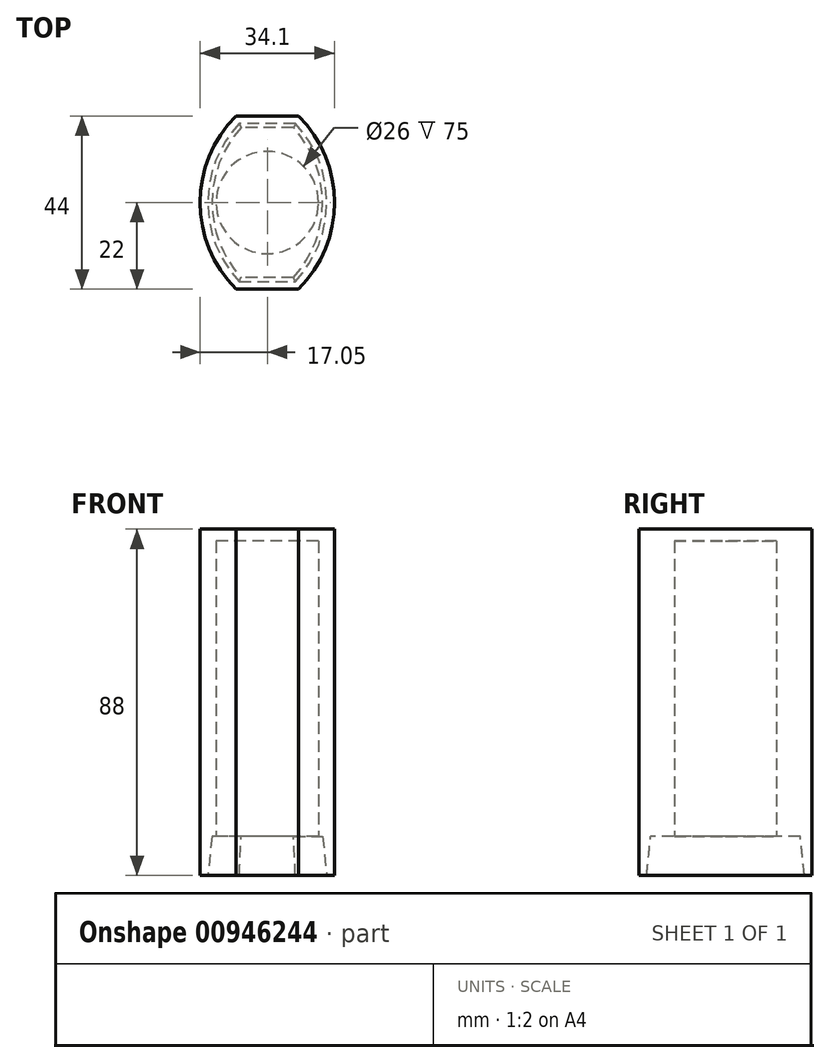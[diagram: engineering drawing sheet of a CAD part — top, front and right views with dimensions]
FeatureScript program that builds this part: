
annotation { "Feature Type Name" : "Feature", "Feature Type Description" : "" }
export const myFeature = defineFeature(function(context is Context, id is Id, definition is map)
    precondition{}
    {
        {
            var Q0;
            Q0=qCreatedBy(makeId("Top.planeOp"),FACE);
            var sketch = newSketch(context, id + "F0", { "sketchPlane" : qUnion([Q0])});
            skLineSegment(sketch, "E0.bottom", {"start": v(6.66, -19) * mm, "end": v(-6.66, -19) * mm});
            skLineSegment(sketch, "E0.top", {"start": v(6.66, 19) * mm, "end": v(-6.66, 19) * mm});
            skLineSegment(sketch, "E0.left", {"start": v(14.1, -19) * mm, "end": v(14.1, 19) * mm, "construction": true});
            skLineSegment(sketch, "E0.right", {"start": v(-14.1, -19) * mm, "end": v(-14.1, 19) * mm, "construction": true});
            skPoint(sketch, "E0.middle", {"position": v(0, 0) * mm});
            skArc(sketch, "E1", {"start": v(-6.66, 19) * mm, "mid": v(-14.05, 0) * mm, "end": v(-6.66, -19) * mm});
            skArc(sketch, "E2.MirrorCS", {"start": v(6.66, 19) * mm, "mid": v(14.05, 0) * mm, "end": v(6.66, -19) * mm});
            skArc(sketch, "E3.0", {"start": v(7.95, 22) * mm, "mid": v(17.05, 0) * mm, "end": v(7.95, -22) * mm});
            skLineSegment(sketch, "E3.1", {"start": v(7.95, 22) * mm, "end": v(-7.95, 22) * mm});
            skArc(sketch, "E3.2", {"start": v(-7.95, 22) * mm, "mid": v(-17.05, 0) * mm, "end": v(-7.95, -22) * mm});
            skLineSegment(sketch, "E3.3", {"start": v(7.95, -22) * mm, "end": v(-7.95, -22) * mm});
            skSolve(sketch);
        }
        {
            var Q0;
            Q0=makeQuery(id+"F0.imprint","IMPRINT",FACE,{"disambiguationData":[TD([[makeQuery(id+"F0.imprint","IMPRINT",EDGE,{"derivedFrom":sQuery(id+"F0.wireOp",EDGE,"E0.bottom")}),1.0]])]});
            extrude(context, id + "F1", {"entities" : qUnion([Q0]), "oppositeDirection" : true, "depth" : 10 * mm, "offsetDistance" : 25 * mm});
        }
        {
            var Q0;
            Q0=makeQuery(id+"F0.imprint","IMPRINT",FACE,{"disambiguationData":[TD([[makeQuery(id+"F0.imprint","IMPRINT",EDGE,{"derivedFrom":sQuery(id+"F0.wireOp",EDGE,"E0.bottom")}),-1.0]])]});
            extrude(context, id + "F2", {"entities" : qUnion([Q0]), "operationType" : NewBodyOperationType.REMOVE, "oppositeDirection" : true, "depth" : 15.1 * mm, "offsetDistance" : 25 * mm, "hasDraft" : true, "draftAngle" : 6 * degree});
        }
        {
            var Q0;
            Q0=makeQuery(id+"F1.opExtrude","CAP_FACE",FACE,{"disambiguationData":[OSD([sQuery(id+"F0.wireOp",EDGE,"E0.bottom"),sQuery(id+"F0.wireOp",EDGE,"E0.top"),sQuery(id+"F0.wireOp",EDGE,"E1"),sQuery(id+"F0.wireOp",EDGE,"E2.MirrorCS"),sQuery(id+"F0.wireOp",EDGE,"E3.0"),sQuery(id+"F0.wireOp",EDGE,"E3.1"),sQuery(id+"F0.wireOp",EDGE,"E3.2"),sQuery(id+"F0.wireOp",EDGE,"E3.3")])],"isStart":true});
            var sketch = newSketch(context, id + "F3", { "sketchPlane" : qUnion([Q0])});
            skCircle(sketch, "E4", {"center": v(0, 0) * mm, "radius": 13 * mm});
            skCircle(sketch, "E5.0", {"center": v(0, 0) * mm, "radius": 16 * mm});
            skLineSegment(sketch, "E6.0.0", {"start": v(-7.95, -22) * mm, "end": v(7.95, -22) * mm});
            skArc(sketch, "E6.0.1", {"start": v(7.95, -22) * mm, "mid": v(17.05, 0) * mm, "end": v(7.95, 22) * mm});
            skLineSegment(sketch, "E6.0.2", {"start": v(7.95, 22) * mm, "end": v(-7.95, 22) * mm});
            skArc(sketch, "E6.0.3", {"start": v(-7.95, 22) * mm, "mid": v(-17.05, 0) * mm, "end": v(-7.95, -22) * mm});
            skArc(sketch, "E7.0.0", {"start": v(6.66, -19) * mm, "mid": v(14.05, 0) * mm, "end": v(6.66, 19) * mm});
            skLineSegment(sketch, "E7.0.1", {"start": v(6.66, 19) * mm, "end": v(-6.66, 19) * mm});
            skArc(sketch, "E7.0.2", {"start": v(-6.66, 19) * mm, "mid": v(-14.05, 0) * mm, "end": v(-6.66, -19) * mm});
            skLineSegment(sketch, "E7.0.3", {"start": v(-6.66, -19) * mm, "end": v(6.66, -19) * mm});
            skSolve(sketch);
        }
        {
            var Q0;
            Q0 = qSketchRegion(id + "F3", true);
            var Q1;
            {var subQ5=sQuery(id+"F3.wireOp",EDGE,"E7.0.1");Q1=makeQuery(id+"F3.imprint","IMPRINT",FACE,{"disambiguationData":[TD([[makeQuery(id+"F3.imprint","IMPRINT",EDGE,{"derivedFrom":subQ5}),1.0]])]});}
            var Q2;
            Q2=makeQuery(id+"F3.imprint","IMPRINT",FACE,{"disambiguationData":[TD([[makeQuery(id+"F3.imprint","IMPRINT",EDGE,{"derivedFrom":sQuery(id+"F3.wireOp",EDGE,"E4")}),-1.0]])]});
            var Q3;
            {var subQ0=sQuery(id+"F3.wireOp",EDGE,"E7.0.0");var subQ1=sQuery(id+"F3.wireOp",EDGE,"E5.0");var subQ2=makeQuery(id+"F3.imprint","INTERSECT",VERTEX,{"disambiguationData":[OD(0.0)],"derivedFrom":[subQ1,subQ0]});Q3=makeQuery(id+"F3.imprint","IMPRINT",FACE,{"disambiguationData":[TD([[makeQuery(id+"F3.imprint","IMPRINT",EDGE,{"disambiguationData":[TD([[subQ2,1.0]])],"derivedFrom":subQ1}),1.0]])]});}
            var Q4;
            Q4=makeQuery(id+"F1.opExtrude","CAP_FACE",FACE,{"disambiguationData":[OSD([sQuery(id+"F0.wireOp",EDGE,"E0.bottom"),sQuery(id+"F0.wireOp",EDGE,"E0.top"),sQuery(id+"F0.wireOp",EDGE,"E1"),sQuery(id+"F0.wireOp",EDGE,"E2.MirrorCS"),sQuery(id+"F0.wireOp",EDGE,"E3.0"),sQuery(id+"F0.wireOp",EDGE,"E3.1"),sQuery(id+"F0.wireOp",EDGE,"E3.2"),sQuery(id+"F0.wireOp",EDGE,"E3.3")])],"isStart":true});
            var Q5;
            {var subQ5=sQuery(id+"F3.wireOp",EDGE,"E7.0.3");Q5=makeQuery(id+"F3.imprint","IMPRINT",FACE,{"disambiguationData":[TD([[makeQuery(id+"F3.imprint","IMPRINT",EDGE,{"derivedFrom":subQ5}),-1.0]])]});}
            extrude(context, id + "F4", {"entities" : qUnion([Q0, Q1, Q2, Q3, Q4, Q5]), "operationType" : NewBodyOperationType.ADD, "depth" : 3 * mm, "offsetDistance" : 25 * mm});
        }
        {
            var Q0;
            {var subQ0=sQuery(id+"F3.wireOp",EDGE,"E7.0.2");var subQ1=sQuery(id+"F3.wireOp",EDGE,"E5.0");var subQ2=makeQuery(id+"F3.imprint","INTERSECT",VERTEX,{"disambiguationData":[OD(0.0)],"derivedFrom":[subQ1,subQ0]});Q0=makeQuery(id+"F3.imprint","IMPRINT",FACE,{"disambiguationData":[TD([[makeQuery(id+"F3.imprint","IMPRINT",EDGE,{"disambiguationData":[TD([[subQ2,-1.0]])],"derivedFrom":subQ1}),1.0]])]});}
            var Q1;
            Q1=makeQuery(id+"F3.imprint","IMPRINT",FACE,{"disambiguationData":[TD([[makeQuery(id+"F3.imprint","IMPRINT",EDGE,{"derivedFrom":sQuery(id+"F3.wireOp",EDGE,"E4")}),-1.0]])]});
            var Q2;
            {var subQ0=sQuery(id+"F3.wireOp",EDGE,"E7.0.0");var subQ1=sQuery(id+"F3.wireOp",EDGE,"E5.0");var subQ2=makeQuery(id+"F3.imprint","INTERSECT",VERTEX,{"disambiguationData":[OD(0.0)],"derivedFrom":[subQ1,subQ0]});Q2=makeQuery(id+"F3.imprint","IMPRINT",FACE,{"disambiguationData":[TD([[makeQuery(id+"F3.imprint","IMPRINT",EDGE,{"disambiguationData":[TD([[subQ2,1.0]])],"derivedFrom":subQ1}),1.0]])]});}
            var Q3;
            Q3=makeQuery(id+"F4.boolean.opBoolean","MERGE",FACE,{"derivedFrom":[makeQuery(id+"F4.opExtrude","CAP_FACE",FACE,{"disambiguationData":[OSD([sQuery(id+"F0.wireOp",EDGE,"E0.bottom"),sQuery(id+"F0.wireOp",EDGE,"E0.top"),sQuery(id+"F0.wireOp",EDGE,"E1"),sQuery(id+"F0.wireOp",EDGE,"E2.MirrorCS"),sQuery(id+"F0.wireOp",EDGE,"E3.0"),sQuery(id+"F0.wireOp",EDGE,"E3.1"),sQuery(id+"F0.wireOp",EDGE,"E3.2"),sQuery(id+"F0.wireOp",EDGE,"E3.3")])],"isStart":false}),makeQuery(id+"F4.opExtrude","CAP_FACE",FACE,{"disambiguationData":[OSD([sQuery(id+"F3.wireOp",EDGE,"E4"),sQuery(id+"F3.wireOp",EDGE,"E5.0"),sQuery(id+"F3.wireOp",EDGE,"E6.0.0"),sQuery(id+"F3.wireOp",EDGE,"E6.0.1"),sQuery(id+"F3.wireOp",EDGE,"E6.0.2"),sQuery(id+"F3.wireOp",EDGE,"E6.0.3"),sQuery(id+"F3.wireOp",EDGE,"E7.0.2")])],"isStart":false})]});
            extrude(context, id + "F5", {"entities" : qUnion([Q0, Q1, Q2, Q3]), "operationType" : NewBodyOperationType.ADD, "depth" : 72 * mm, "offsetDistance" : 25 * mm});
        }
        {
            var Q0;
            Q0=makeQuery(id+"F5.opExtrude","CAP_FACE",FACE,{"disambiguationData":[OSD([sQuery(id+"F0.wireOp",EDGE,"E0.bottom"),sQuery(id+"F0.wireOp",EDGE,"E0.top"),sQuery(id+"F0.wireOp",EDGE,"E1"),sQuery(id+"F0.wireOp",EDGE,"E2.MirrorCS"),sQuery(id+"F0.wireOp",EDGE,"E3.0"),sQuery(id+"F0.wireOp",EDGE,"E3.1"),sQuery(id+"F0.wireOp",EDGE,"E3.2"),sQuery(id+"F0.wireOp",EDGE,"E3.3"),sQuery(id+"F3.wireOp",EDGE,"E4"),sQuery(id+"F3.wireOp",EDGE,"E5.0"),sQuery(id+"F3.wireOp",EDGE,"E6.0.0"),sQuery(id+"F3.wireOp",EDGE,"E6.0.1"),sQuery(id+"F3.wireOp",EDGE,"E6.0.2"),sQuery(id+"F3.wireOp",EDGE,"E6.0.3"),sQuery(id+"F3.wireOp",EDGE,"E7.0.2")])],"isStart":false});
            var sketch = newSketch(context, id + "F6", { "sketchPlane" : qUnion([Q0])});
            skLineSegment(sketch, "E8.0.0", {"start": v(-7.95, -22) * mm, "end": v(7.95, -22) * mm});
            skArc(sketch, "E8.0.1", {"start": v(7.95, -22) * mm, "mid": v(17.05, 0) * mm, "end": v(7.95, 22) * mm});
            skLineSegment(sketch, "E8.0.2", {"start": v(7.95, 22) * mm, "end": v(-7.95, 22) * mm});
            skArc(sketch, "E8.0.3", {"start": v(-7.95, 22) * mm, "mid": v(-17.05, 0) * mm, "end": v(-7.95, -22) * mm});
            skSolve(sketch);
        }
        {
            var Q0;
            Q0 = qSketchRegion(id + "F6", true);
            extrude(context, id + "F7", {"entities" : qUnion([Q0]), "operationType" : NewBodyOperationType.ADD, "depth" : 3 * mm, "offsetDistance" : 25 * mm});
        }
    });
